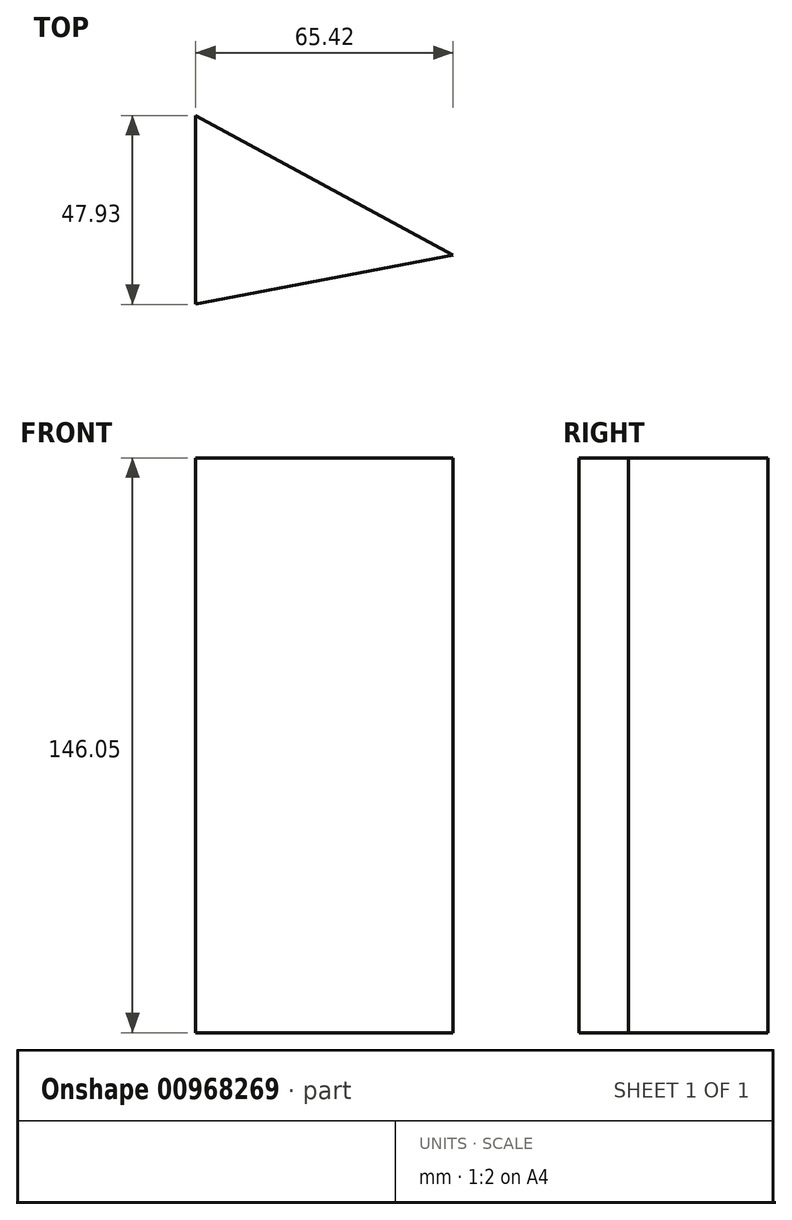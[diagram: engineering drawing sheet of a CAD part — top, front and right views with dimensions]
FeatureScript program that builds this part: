
annotation { "Feature Type Name" : "Feature", "Feature Type Description" : "" }
export const myFeature = defineFeature(function(context is Context, id is Id, definition is map)
    precondition{}
    {
        {
            var Q0;
            Q0=qCreatedBy(makeId("Top.planeOp"), FACE);
            var sketch = newSketch(context, id + "F0", { "sketchPlane" : qUnion([Q0])});
            skLineSegment(sketch, "E0", {"start": v(0, 0) * mm, "end": v(65.42, -35.37) * mm});
            skLineSegment(sketch, "E1", {"start": v(65.42, -35.37) * mm, "end": v(0, -47.93) * mm});
            skLineSegment(sketch, "E2", {"start": v(0, -47.93) * mm, "end": v(0, 0) * mm});
            skSolve(sketch);
        }
        {
            var Q0;
            Q0 = qSketchRegion(id + "F0", true);
            extrude(context, id + "F1", {"entities" : qUnion([Q0]), "domain" : OperationDomain.MODEL, "flatOperationType" : FlatOperationType.REMOVE, "depth" : 146.05 * mm, "offsetDistance" : 25.4 * mm});
        }
    });
